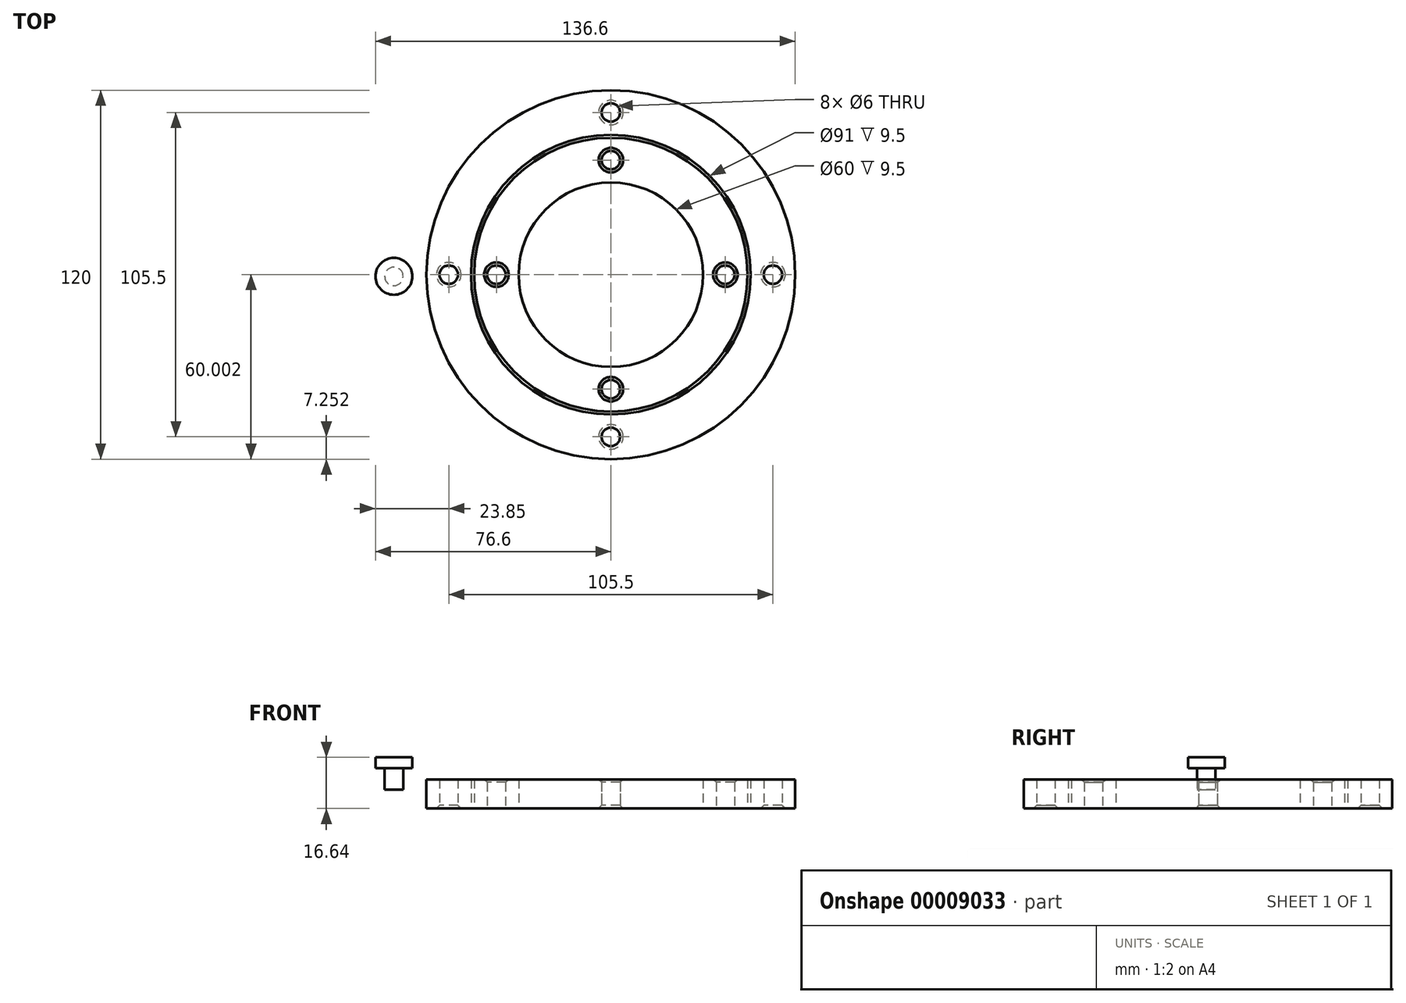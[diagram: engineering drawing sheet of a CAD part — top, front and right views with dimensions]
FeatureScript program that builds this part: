
annotation { "Feature Type Name" : "Feature", "Feature Type Description" : "" }
export const myFeature = defineFeature(function(context is Context, id is Id, definition is map)
    precondition{}
    {
        {
            var Q0;
            Q0=qCreatedBy(makeId("Top.planeOp"),FACE);
            var sketch = newSketch(context, id + "F0", { "sketchPlane" : qUnion([Q0])});
            skCircle(sketch, "E0", {"center": v(4.25, 0.54) * mm, "radius": 60 * mm});
            skCircle(sketch, "E1", {"center": v(4.25, 0.54) * mm, "radius": 30 * mm});
            skCircle(sketch, "E2", {"center": v(4.25, 0.54) * mm, "radius": 45 * mm, "construction": true});
            skCircle(sketch, "E3.0", {"center": v(4.25, 0.54) * mm, "radius": 45.5 * mm});
            skCircle(sketch, "E4.0", {"center": v(4.25, 0.54) * mm, "radius": 44.5 * mm});
            skLineSegment(sketch, "E5", {"start": v(4.25, 60.54) * mm, "end": v(4.25, 46.04) * mm, "construction": true});
            skLineSegment(sketch, "E6", {"start": v(4.25, 30.54) * mm, "end": v(4.25, 45.04) * mm, "construction": true});
            skCircle(sketch, "E7", {"center": v(4.25, 53.3) * mm, "radius": 3 * mm});
            skCircle(sketch, "E8", {"center": v(4.25, 37.8) * mm, "radius": 3 * mm});
            skLineSegment(sketch, "E9", {"start": v(34.25, 0.54) * mm, "end": v(48.75, 0.54) * mm, "construction": true});
            skLineSegment(sketch, "E10", {"start": v(49.75, 0.54) * mm, "end": v(64.25, 0.54) * mm, "construction": true});
            skCircle(sketch, "E11", {"center": v(57, 0.54) * mm, "radius": 3 * mm});
            skCircle(sketch, "E12", {"center": v(41.5, 0.54) * mm, "radius": 3 * mm});
            skLineSegment(sketch, "E13", {"start": v(4.25, -29.46) * mm, "end": v(4.25, -43.96) * mm, "construction": true});
            skLineSegment(sketch, "E14", {"start": v(4.25, -44.96) * mm, "end": v(4.25, -59.46) * mm, "construction": true});
            skLineSegment(sketch, "E15", {"start": v(-41.25, 0.54) * mm, "end": v(-55.75, 0.54) * mm, "construction": true});
            skLineSegment(sketch, "E16", {"start": v(-25.75, 0.54) * mm, "end": v(-40.25, 0.54) * mm, "construction": true});
            skCircle(sketch, "E17", {"center": v(4.25, -36.7) * mm, "radius": 3 * mm});
            skCircle(sketch, "E18", {"center": v(4.25, -52.2) * mm, "radius": 3 * mm});
            skCircle(sketch, "E19", {"center": v(-33, 0.54) * mm, "radius": 3 * mm});
            skCircle(sketch, "E20", {"center": v(-48.5, 0.54) * mm, "radius": 3 * mm});
            skSolve(sketch);
        }
        {
            var Q0;
            Q0=makeQuery(id+"F0.imprint","IMPRINT",FACE,{"disambiguationData":[TD([[makeQuery(id+"F0.imprint","IMPRINT",EDGE,{"derivedFrom":sQuery(id+"F0.wireOp",EDGE,"E0")}),1.0]])]});
            var Q1;
            Q1=makeQuery(id+"F0.imprint","IMPRINT",FACE,{"disambiguationData":[TD([[makeQuery(id+"F0.imprint","IMPRINT",EDGE,{"derivedFrom":sQuery(id+"F0.wireOp",EDGE,"E1")}),-1.0]])]});
            extrude(context, id + "F1", {"entities" : qUnion([Q0, Q1]), "depth" : 9.5 * mm});
        }
        {
            var Q0;
            Q0=makeQuery(id+"F1.opExtrude","CAP_EDGE",EDGE,{"disambiguationData":[OSD([sQuery(id+"F0.wireOp",EDGE,"E8")])],"isStart":false});
            var Q1;
            Q1=makeQuery(id+"F1.opExtrude","CAP_EDGE",EDGE,{"disambiguationData":[OSD([sQuery(id+"F0.wireOp",EDGE,"E19")])],"isStart":false});
            var Q2;
            Q2=makeQuery(id+"F1.opExtrude","CAP_EDGE",EDGE,{"disambiguationData":[OSD([sQuery(id+"F0.wireOp",EDGE,"E17")])],"isStart":false});
            var Q3;
            Q3=makeQuery(id+"F1.opExtrude","CAP_EDGE",EDGE,{"disambiguationData":[OSD([sQuery(id+"F0.wireOp",EDGE,"E12")])],"isStart":false});
            var Q4;
            Q4=makeQuery(id+"F1.opExtrude","CAP_EDGE",EDGE,{"disambiguationData":[OSD([sQuery(id+"F0.wireOp",EDGE,"E7")])],"isStart":true});
            var Q5;
            Q5=makeQuery(id+"F1.opExtrude","CAP_EDGE",EDGE,{"disambiguationData":[OSD([sQuery(id+"F0.wireOp",EDGE,"E11")])],"isStart":true});
            var Q6;
            Q6=makeQuery(id+"F1.opExtrude","CAP_EDGE",EDGE,{"disambiguationData":[OSD([sQuery(id+"F0.wireOp",EDGE,"E20")])],"isStart":true});
            var Q7;
            Q7=makeQuery(id+"F1.opExtrude","CAP_EDGE",EDGE,{"disambiguationData":[OSD([sQuery(id+"F0.wireOp",EDGE,"E18")])],"isStart":true});
            chamfer(context, id + "F2", {"entities" : qUnion([Q0, Q1, Q2, Q3, Q4, Q5, Q6, Q7]), "width" : 1 * mm, "tangentPropagation" : true});
        }
        {
            var Q0;
            Q0=qCreatedBy(makeId("Front.planeOp"),FACE);
            var sketch = newSketch(context, id + "F3", { "sketchPlane" : qUnion([Q0])});
            skLineSegment(sketch, "E21", {"start": v(-66.35, 6.14) * mm, "end": v(-66.35, 16.64) * mm});
            skLineSegment(sketch, "E22", {"start": v(-72.35, 16.64) * mm, "end": v(-72.35, 13.14) * mm});
            skLineSegment(sketch, "E23", {"start": v(-69.35, 13.14) * mm, "end": v(-72.35, 13.14) * mm});
            skLineSegment(sketch, "E24", {"start": v(-69.35, 13.14) * mm, "end": v(-69.35, 6.14) * mm});
            skLineSegment(sketch, "E25", {"start": v(-69.35, 6.14) * mm, "end": v(-66.35, 6.14) * mm});
            skLineSegment(sketch, "E26", {"start": v(-72.35, 16.64) * mm, "end": v(-66.35, 16.64) * mm});
            skSolve(sketch);
        }
        {
            var Q0;
            Q0=makeQuery(id+"F3.imprint","IMPRINT",FACE,{"disambiguationData":[TD([[makeQuery(id+"F3.imprint","IMPRINT",EDGE,{"derivedFrom":sQuery(id+"F3.wireOp",EDGE,"E21")}),1.0]])]});
            var Q1;
            Q1=sQuery(id+"F3.wireOp",EDGE,"E21");
            revolve(context, id + "F4", {"entities" : qUnion([Q0]), "axis" : qUnion([Q1]), "revolveType" : RevolveType.FULL});
        }
    });
